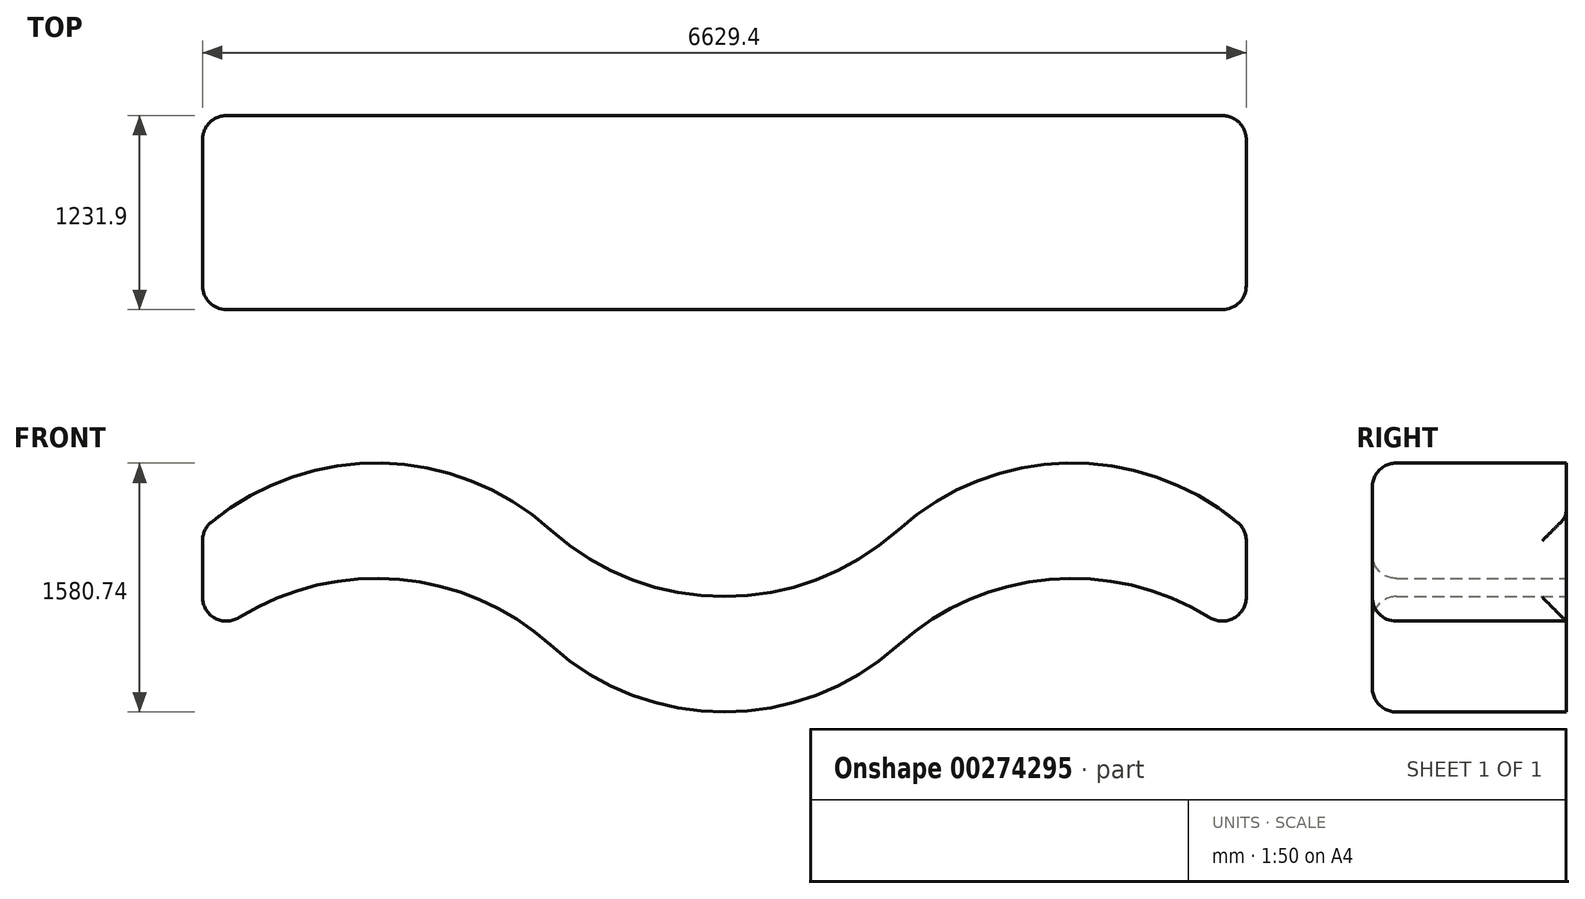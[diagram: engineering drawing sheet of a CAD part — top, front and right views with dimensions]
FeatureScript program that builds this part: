
annotation { "Feature Type Name" : "Feature", "Feature Type Description" : "" }
export const myFeature = defineFeature(function(context is Context, id is Id, definition is map)
    precondition{}
    {
        {
            var Q0;
            Q0=qCreatedBy(makeId("Front.planeOp"),FACE);
            var sketch = newSketch(context, id + "F0", { "sketchPlane" : qUnion([Q0])});
            skLineSegment(sketch, "E0", {"start": v(0, 0) * mm, "end": v(2209.8, 0) * mm});
            skLineSegment(sketch, "E1", {"start": v(2209.8, 0) * mm, "end": v(0, 0) * mm});
            skLineSegment(sketch, "E2", {"start": v(-2209.8, 0) * mm, "end": v(0, 0) * mm});
            skLineSegment(sketch, "E3", {"start": v(-2209.8, 0) * mm, "end": v(-4419.6, 0) * mm});
            skLineSegment(sketch, "E4", {"start": v(-4419.6, 0) * mm, "end": v(-4419.6, 732.3) * mm});
            skLineSegment(sketch, "E5", {"start": v(-2209.8, 0) * mm, "end": v(-2209.8, 732.3) * mm});
            skLineSegment(sketch, "E6", {"start": v(0, 0) * mm, "end": v(0, 732.3) * mm});
            skLineSegment(sketch, "E7", {"start": v(2209.8, 0) * mm, "end": v(2209.8, 732.3) * mm});
            skArc(sketch, "E8", {"start": v(-2209.8, 732.3) * mm, "mid": v(-3314.7, 1156.52) * mm, "end": v(-4419.6, 732.3) * mm});
            skArc(sketch, "E9", {"start": v(-2209.8, 0) * mm, "mid": v(-3314.7, 424.22) * mm, "end": v(-4419.6, 0) * mm});
            skArc(sketch, "E10", {"start": v(-2209.8, 0) * mm, "mid": v(-1104.9, -424.22) * mm, "end": v(0, 0) * mm});
            skArc(sketch, "E11", {"start": v(-2209.8, 732.3) * mm, "mid": v(-1104.9, 308.08) * mm, "end": v(0, 732.3) * mm});
            skArc(sketch, "E12", {"start": v(2209.8, 732.3) * mm, "mid": v(1104.9, 1156.52) * mm, "end": v(0, 732.3) * mm});
            skArc(sketch, "E13", {"start": v(2209.8, 0) * mm, "mid": v(1104.9, 424.22) * mm, "end": v(0, 0) * mm});
            skSolve(sketch);
        }
        {
            var Q0;
            Q0=makeQuery(id+"F0.imprint","IMPRINT",FACE,{"disambiguationData":[TD([[makeQuery(id+"F0.imprint","IMPRINT",EDGE,{"derivedFrom":sQuery(id+"F0.wireOp",EDGE,"E4")}),-1.0]])]});
            var Q1;
            Q1=makeQuery(id+"F0.imprint","IMPRINT",FACE,{"disambiguationData":[TD([[makeQuery(id+"F0.imprint","IMPRINT",EDGE,{"derivedFrom":sQuery(id+"F0.wireOp",EDGE,"E2")}),1.0]])]});
            var Q2;
            Q2=makeQuery(id+"F0.imprint","IMPRINT",FACE,{"disambiguationData":[TD([[makeQuery(id+"F0.imprint","IMPRINT",EDGE,{"derivedFrom":sQuery(id+"F0.wireOp",EDGE,"E2")}),-1.0]])]});
            var Q3;
            Q3=makeQuery(id+"F0.imprint","IMPRINT",FACE,{"disambiguationData":[TD([[makeQuery(id+"F0.imprint","IMPRINT",EDGE,{"derivedFrom":sQuery(id+"F0.wireOp",EDGE,"E6")}),-1.0]])]});
            extrude(context, id + "F1", {"entities" : qUnion([Q0, Q1, Q2, Q3]), "depth" : 1231.9 * mm});
        }
        {
            var Q0;
            Q0=makeQuery(id+"F1.opExtrude","CAP_FACE",FACE,{"disambiguationData":[OSD([sQuery(id+"F0.wireOp",EDGE,"E4"),sQuery(id+"F0.wireOp",EDGE,"E7"),sQuery(id+"F0.wireOp",EDGE,"E8"),sQuery(id+"F0.wireOp",EDGE,"E9"),sQuery(id+"F0.wireOp",EDGE,"E10"),sQuery(id+"F0.wireOp",EDGE,"E11"),sQuery(id+"F0.wireOp",EDGE,"E12"),sQuery(id+"F0.wireOp",EDGE,"E13")])],"isStart":false});
            var Q1;
            Q1=makeQuery(id+"F1.opExtrude","SWEPT_FACE",FACE,{"disambiguationData":[OSD([sQuery(id+"F0.wireOp",EDGE,"E7")])]});
            var Q2;
            Q2=makeQuery(id+"F1.opExtrude","SWEPT_FACE",FACE,{"disambiguationData":[OSD([sQuery(id+"F0.wireOp",EDGE,"E4")])]});
            fillet(context, id + "F2", {"entities" : qUnion([Q0, Q1, Q2]), "radius" : 152.4 * mm, "tangentPropagation" : true, "allowEdgeOverflow" : false});
        }
    });
